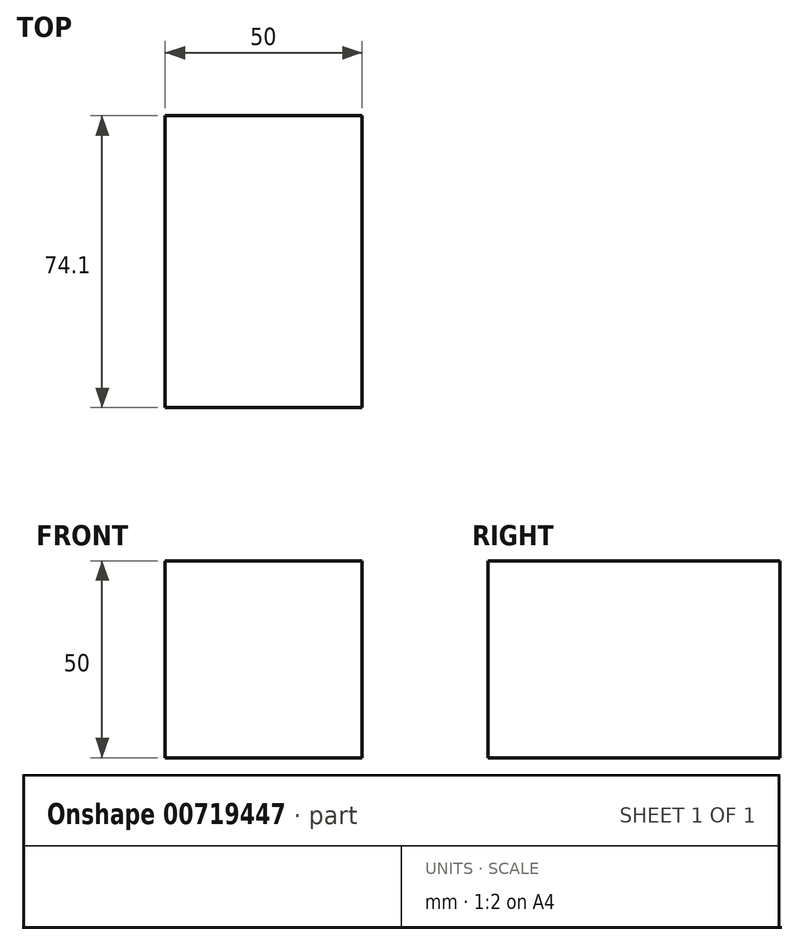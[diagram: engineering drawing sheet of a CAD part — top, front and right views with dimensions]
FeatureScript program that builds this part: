
annotation { "Feature Type Name" : "Feature", "Feature Type Description" : "" }
export const myFeature = defineFeature(function(context is Context, id is Id, definition is map)
    precondition{}
    {
        {
            var Q0;
            Q0=qCreatedBy(makeId("Front.planeOp"),FACE);
            var sketch = newSketch(context, id + "F0", { "sketchPlane" : qUnion([Q0])});
            skLineSegment(sketch, "E0.bottom", {"start": v(-25, 25) * mm, "end": v(25, 25) * mm});
            skLineSegment(sketch, "E0.top", {"start": v(-25, -25) * mm, "end": v(25, -25) * mm});
            skLineSegment(sketch, "E0.left", {"start": v(-25, 25) * mm, "end": v(-25, -25) * mm});
            skLineSegment(sketch, "E0.right", {"start": v(25, 25) * mm, "end": v(25, -25) * mm});
            skSolve(sketch);
        }
        {
            var Q0;
            Q0=makeQuery(id+"F0.imprint","IMPRINT",FACE,{"disambiguationData":[TD([[makeQuery(id+"F0.imprint","IMPRINT",EDGE,{"derivedFrom":sQuery(id+"F0.wireOp",EDGE,"E0.bottom")}),-1.0]])]});
            extrude(context, id + "F1", {"entities" : qUnion([Q0]), "endBound" : BoundingType.SYMMETRIC, "depth" : 74.1 * mm, "offsetDistance" : 25 * mm});
        }
    });
